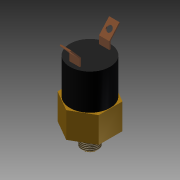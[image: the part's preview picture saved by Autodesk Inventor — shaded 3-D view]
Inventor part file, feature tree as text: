
AUTODESK INVENTOR PART (.ipt)
format: ipt  version: 2014 (Build 180170000, 170)  size: 161,792 bytes
history: native  units: mm (DEFAULTED — no unit token found)
features: extrude x6, sketch x6, projected_geometry x4, mirror x1, thread x1, chamfer x1, fillet x1
ambient origin geometry x8: Origin, YZ Plane, XZ Plane, XY Plane, X Axis, Y Axis, Z Axis, Center Point
bodies: Solid1 (feature_tree)
feature tree (20):
  extrude  "Extrusion1"  Depth=15.875mm TaperAngle=0.0deg
  extrude  "Extrusion2"  Depth=11.049mm TaperAngle=0.0deg
  extrude  "Extrusion3"  Depth=19.9898mm TaperAngle=0.0deg
  extrude  "Extrusion4"  Depth=21.971mm TaperAngle=0.0deg
  extrude  "Extrusion5"  Depth=0.762mm
  extrude  "Extrusion6"  Depth=3.175mm
  mirror  "Mirror1"
  thread  "Thread1"  [1 undecoded]
  chamfer  "Chamfer1"  Distance=6.35mm
  fillet  "Fillet1"  Radius=6.35mm
  sketch  "Sketch1"  dims[d0=25.4mm d1=15.875mm d2=0.0mm]
  sketch  "Sketch2"  dims[d3=10.16mm d4=11.049mm d5=0.0mm]
  projected_geometry  "Projected Loop1"
  sketch  "Sketch3"  dims[d6=3.175mm d7=19.9898mm d8=0.0mm]
  sketch  "Sketch4"  dims[d9=24.765mm d10=21.971mm d11=0.0mm]
  projected_geometry  "Projected Loop2"
  sketch  "Sketch5"  dims[d12=19.05mm d13=0.762mm]
  projected_geometry  "Projected Loop3"
  sketch  "Sketch6"  dims[d14=0.762mm d15=4.699mm d17=9.398mm d18=6.35mm d19=0.0mm d20=6.35mm d21=0.0mm d22=25.4mm d23=0.0mm d24=1.0mm d25=3.175mm d26=45.0deg d27=3.175mm]
  projected_geometry  "Projected Loop4"
note: 1 required parameter value undecoded (feature->parameter linkage not recoverable at this tier; creation-order binding heuristic only, values carry confidence <= 0.55)
